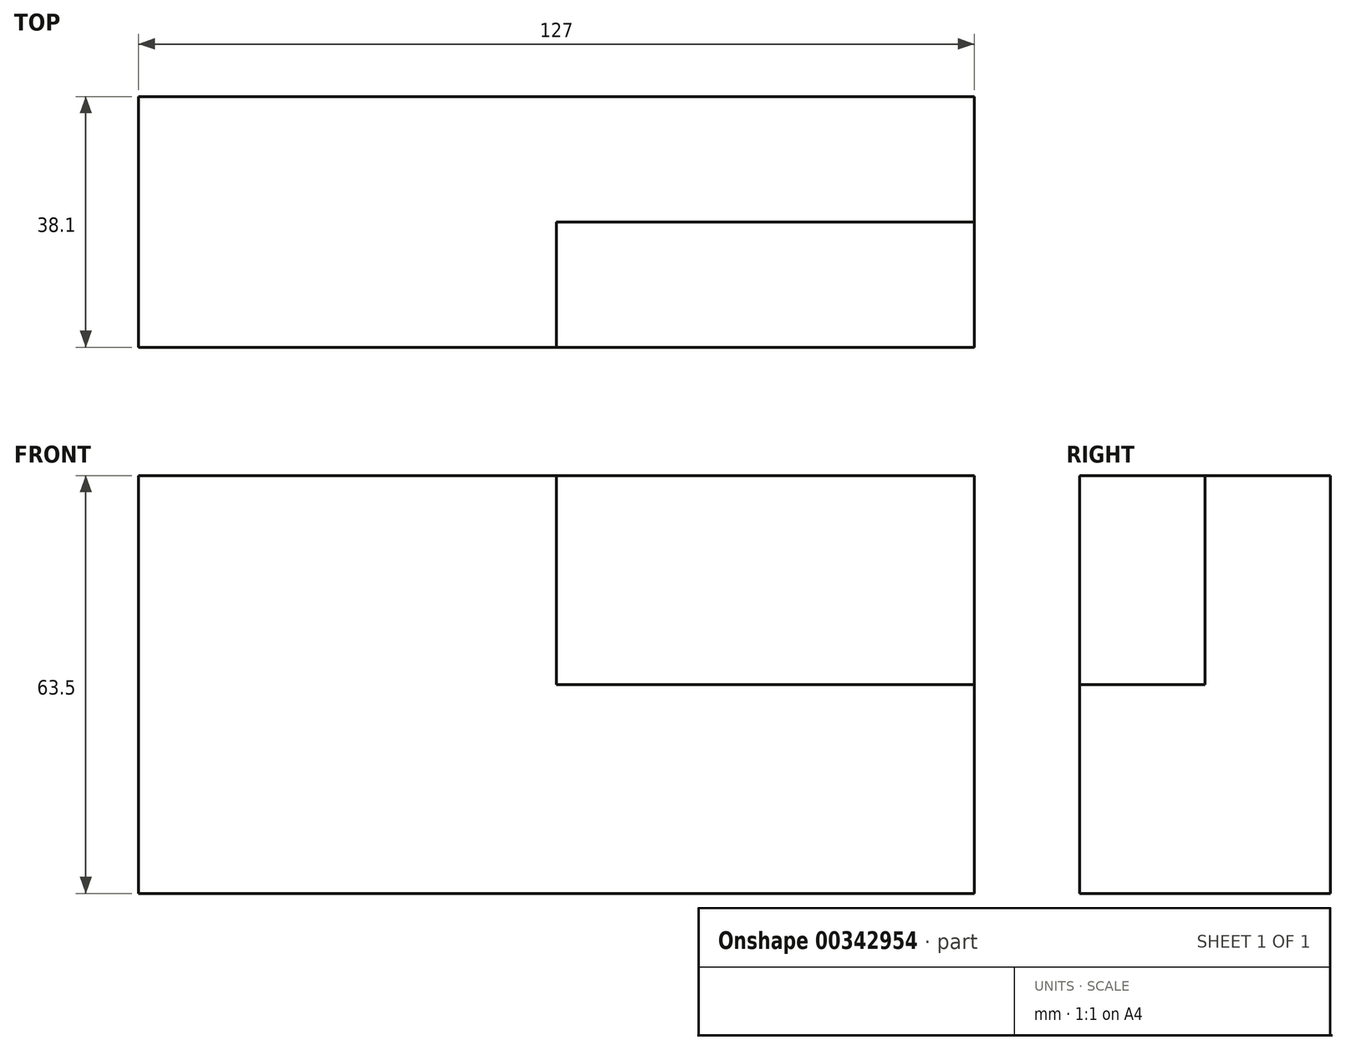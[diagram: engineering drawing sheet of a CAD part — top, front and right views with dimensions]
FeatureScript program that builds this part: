
annotation { "Feature Type Name" : "Feature", "Feature Type Description" : "" }
export const myFeature = defineFeature(function(context is Context, id is Id, definition is map)
    precondition{}
    {
        {
            var Q0;
            Q0=qCreatedBy(makeId("Front.planeOp"),FACE);
            var sketch = newSketch(context, id + "F0", { "sketchPlane" : qUnion([Q0])});
            skLineSegment(sketch, "E0", {"start": v(-75.6, 74.43) * mm, "end": v(51.4, 74.43) * mm});
            skLineSegment(sketch, "E1", {"start": v(-75.6, 74.43) * mm, "end": v(-75.6, 10.93) * mm});
            skLineSegment(sketch, "E2", {"start": v(-75.6, 10.93) * mm, "end": v(51.4, 10.93) * mm});
            skLineSegment(sketch, "E3", {"start": v(51.4, 10.93) * mm, "end": v(51.4, 74.43) * mm});
            skLineSegment(sketch, "E4.bottom", {"start": v(-12.1, 74.43) * mm, "end": v(51.4, 74.43) * mm});
            skLineSegment(sketch, "E4.top", {"start": v(-12.1, 42.68) * mm, "end": v(51.4, 42.68) * mm});
            skLineSegment(sketch, "E4.left", {"start": v(-12.1, 74.43) * mm, "end": v(-12.1, 42.68) * mm});
            skLineSegment(sketch, "E4.right", {"start": v(51.4, 74.43) * mm, "end": v(51.4, 42.68) * mm});
            skSolve(sketch);
        }
        {
            var Q0;
            {var subQ3=sQuery(id+"F0.wireOp",EDGE,"E1");Q0=makeQuery(id+"F0.imprint","IMPRINT",FACE,{"disambiguationData":[TD([[makeQuery(id+"F0.imprint","IMPRINT",EDGE,{"derivedFrom":subQ3}),1.0]])]});}
            extrude(context, id + "F1", {"entities" : qUnion([Q0]), "depth" : 38.1 * mm});
        }
        {
            var Q0;
            {var subQ2=sQuery(id+"F0.wireOp",EDGE,"E4.top");var subQ4=sQuery(id+"F0.wireOp",EDGE,"E1");var subQ8=makeQuery(id+"F0.imprint","IMPRINT",EDGE,{"derivedFrom":subQ2});Q0=qUnion([makeQuery(id+"F0.imprint","IMPRINT",FACE,{"disambiguationData":[TD([[subQ8,1.0]])]}),makeQuery(id+"F0.imprint","IMPRINT",FACE,{"disambiguationData":[TD([[makeQuery(id+"F0.imprint","IMPRINT",EDGE,{"derivedFrom":subQ4}),1.0]])]})]);}
            extrude(context, id + "F2", {"entities" : qUnion([Q0]), "operationType" : NewBodyOperationType.ADD, "depth" : 19.05 * mm});
        }
    });
